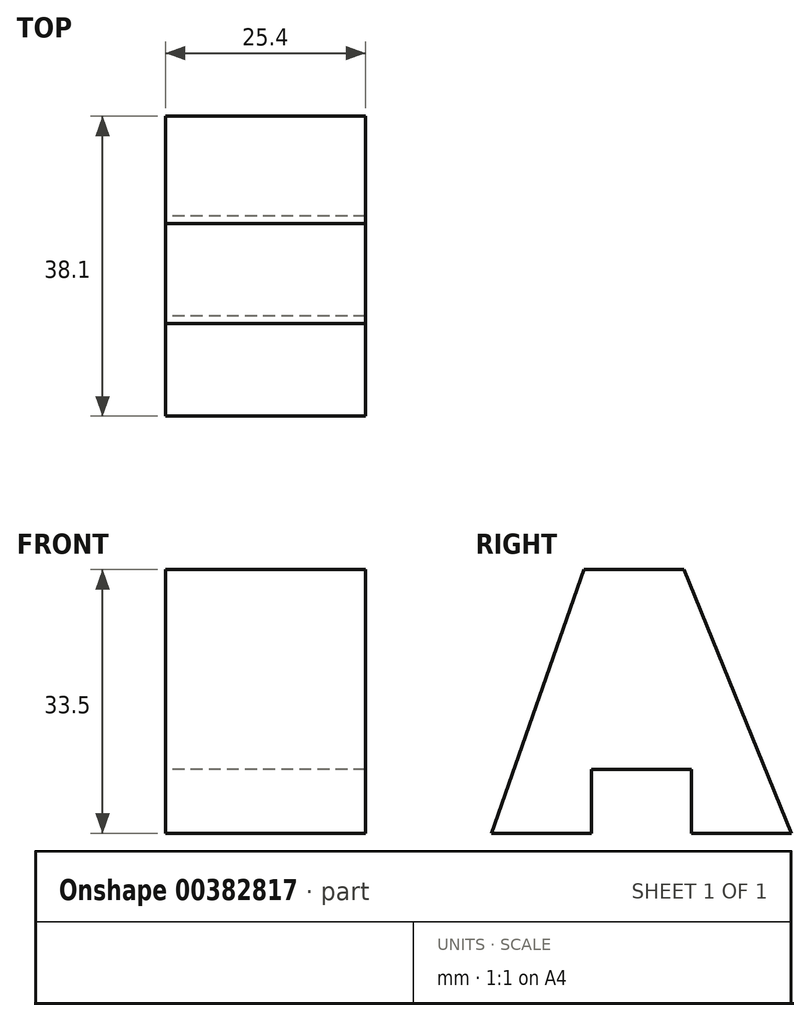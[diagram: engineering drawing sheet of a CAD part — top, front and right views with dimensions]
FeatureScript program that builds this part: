
annotation { "Feature Type Name" : "Feature", "Feature Type Description" : "" }
export const myFeature = defineFeature(function(context is Context, id is Id, definition is map)
    precondition{}
    {
        {
            var Q0;
            Q0=qCreatedBy(makeId("Right.planeOp"),FACE);
            var sketch = newSketch(context, id + "F0", { "sketchPlane" : qUnion([Q0])});
            skLineSegment(sketch, "E0", {"start": v(14.29, 0) * mm, "end": v(26.03, 33.5) * mm});
            skLineSegment(sketch, "E1", {"start": v(26.03, 33.5) * mm, "end": v(38.73, 33.5) * mm});
            skLineSegment(sketch, "E2", {"start": v(38.73, 33.5) * mm, "end": v(52.39, 0) * mm});
            skLineSegment(sketch, "E3", {"start": v(52.39, 0) * mm, "end": v(39.69, 0) * mm});
            skLineSegment(sketch, "E4", {"start": v(39.69, 0) * mm, "end": v(39.69, 8.1) * mm});
            skLineSegment(sketch, "E5", {"start": v(39.69, 8.1) * mm, "end": v(26.99, 8.1) * mm});
            skLineSegment(sketch, "E6", {"start": v(26.99, 8.1) * mm, "end": v(26.99, 0) * mm});
            skLineSegment(sketch, "E7", {"start": v(26.99, 0) * mm, "end": v(14.29, 0) * mm});
            skSolve(sketch);
        }
        {
            var Q0;
            Q0 = qSketchRegion(id + "F0", true);
            extrude(context, id + "F1", {"entities" : qUnion([Q0]), "depth" : 25.4 * mm});
        }
    });
